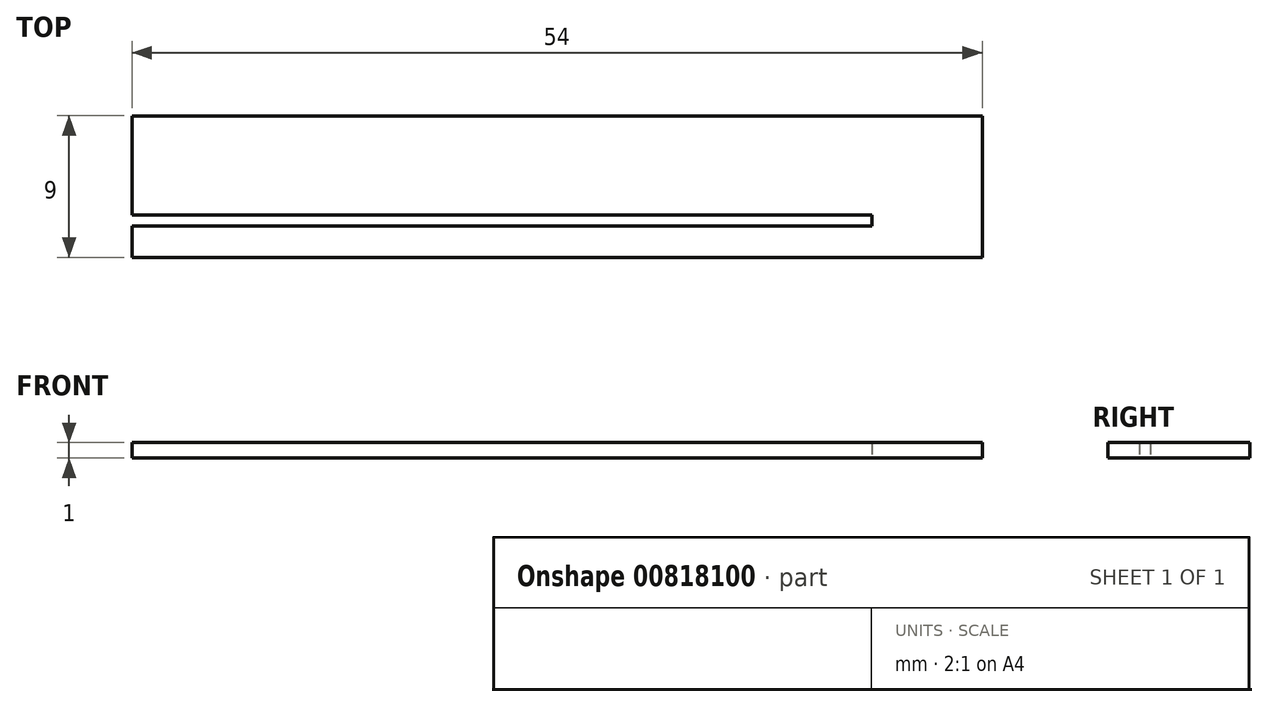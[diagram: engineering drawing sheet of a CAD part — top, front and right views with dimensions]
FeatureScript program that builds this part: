
annotation { "Feature Type Name" : "Feature", "Feature Type Description" : "" }
export const myFeature = defineFeature(function(context is Context, id is Id, definition is map)
    precondition{}
    {
        {
            assignVariable(context, id + "F0", {"name" : "credit_card_thickness", "anyValue" : 1});
        }
        {
            var Q0;
            Q0=qCreatedBy(makeId("Top.planeOp"),FACE);
            var sketch = newSketch(context, id + "F1", { "sketchPlane" : qUnion([Q0])});
            skLineSegment(sketch, "E0.bottom", {"start": v(-32.38, -4.72) * mm, "end": v(21.62, -4.72) * mm});
            skLineSegment(sketch, "E0.top", {"start": v(-32.38, -13.72) * mm, "end": v(21.62, -13.72) * mm});
            skLineSegment(sketch, "E0.left", {"start": v(-32.38, -4.72) * mm, "end": v(-32.38, -11.02) * mm});
            skLineSegment(sketch, "E0.right", {"start": v(21.62, -4.72) * mm, "end": v(21.62, -13.72) * mm});
            skLineSegment(sketch, "E1.bottom", {"start": v(-32.38, -11.02) * mm, "end": v(14.62, -11.02) * mm});
            skLineSegment(sketch, "E1.top", {"start": v(-32.38, -11.72) * mm, "end": v(14.62, -11.72) * mm});
            skLineSegment(sketch, "E1.right", {"start": v(14.62, -11.02) * mm, "end": v(14.62, -11.72) * mm});
            skLineSegment(sketch, "E2.trimOffspring", {"start": v(-32.38, -11.72) * mm, "end": v(-32.38, -13.72) * mm});
            skSolve(sketch);
        }
        {
            var Q0;
            Q0 = qSketchRegion(id + "F1", true);
            extrude(context, id + "F2", {"entities" : qUnion([Q0]), "depth" : (getVariable(context, 'credit_card_thickness')) * mm, "offsetDistance" : 25 * mm});
        }
    });
